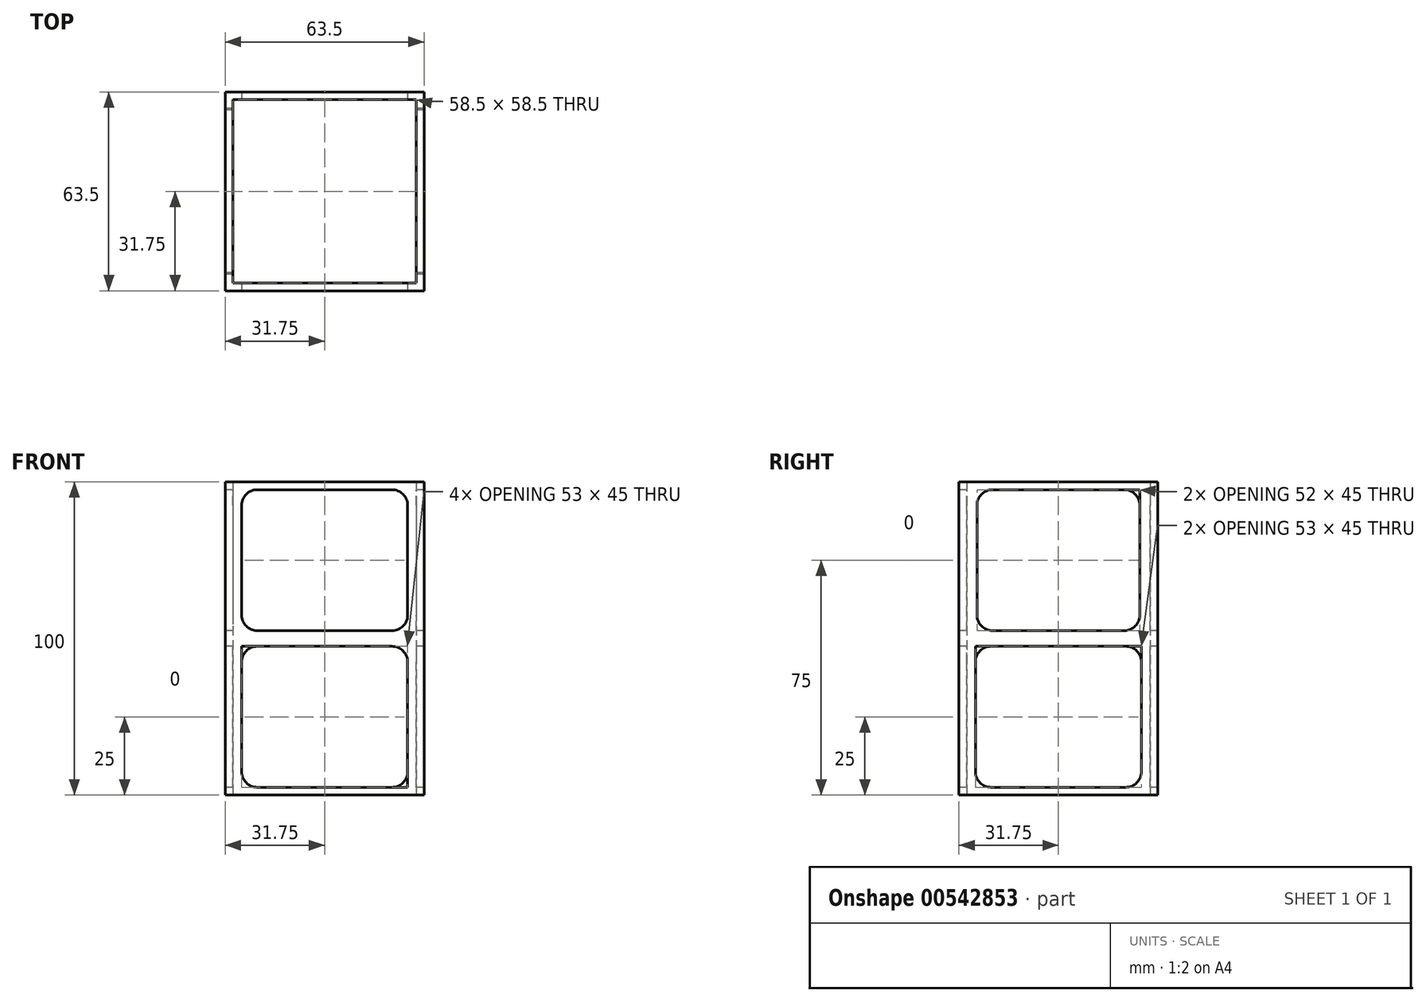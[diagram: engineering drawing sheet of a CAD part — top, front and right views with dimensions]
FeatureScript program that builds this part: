
annotation { "Feature Type Name" : "Feature", "Feature Type Description" : "" }
export const myFeature = defineFeature(function(context is Context, id is Id, definition is map)
    precondition{}
    {
        {
            var Q0;
            Q0=qCreatedBy(makeId("Top.planeOp"),FACE);
            var sketch = newSketch(context, id + "F0", { "sketchPlane" : qUnion([Q0])});
            skLineSegment(sketch, "E0.bottom", {"start": v(31.75, -31.75) * mm, "end": v(-31.75, -31.75) * mm});
            skLineSegment(sketch, "E0.top", {"start": v(31.75, 31.75) * mm, "end": v(-31.75, 31.75) * mm});
            skLineSegment(sketch, "E0.left", {"start": v(31.75, -31.75) * mm, "end": v(31.75, 31.75) * mm});
            skLineSegment(sketch, "E0.right", {"start": v(-31.75, -31.75) * mm, "end": v(-31.75, 31.75) * mm});
            skPoint(sketch, "E0.middle", {"position": v(0, 0) * mm});
            skLineSegment(sketch, "E1.bottom", {"start": v(29.25, -29.25) * mm, "end": v(-29.25, -29.25) * mm});
            skLineSegment(sketch, "E1.top", {"start": v(29.25, 29.25) * mm, "end": v(-29.25, 29.25) * mm});
            skLineSegment(sketch, "E1.left", {"start": v(29.25, -29.25) * mm, "end": v(29.25, 29.25) * mm});
            skLineSegment(sketch, "E1.right", {"start": v(-29.25, -29.25) * mm, "end": v(-29.25, 29.25) * mm});
            skSolve(sketch);
        }
        {
            var Q0;
            Q0=makeQuery(id+"F0.imprint","IMPRINT",FACE,{"disambiguationData":[TD([[makeQuery(id+"F0.imprint","IMPRINT",EDGE,{"derivedFrom":sQuery(id+"F0.wireOp",EDGE,"E0.bottom")}),-1.0]])]});
            extrude(context, id + "F1", {"entities" : qUnion([Q0]), "depth" : 100 * mm, "offsetDistance" : 25.4 * mm});
        }
        {
            var Q0;
            Q0=makeQuery(id+"F1.opExtrude","SWEPT_FACE",FACE,{"disambiguationData":[OSD([sQuery(id+"F0.wireOp",EDGE,"E0.bottom")])]});
            var sketch = newSketch(context, id + "F2", { "sketchPlane" : qUnion([Q0])});
            skLineSegment(sketch, "E2.bottom", {"start": v(26.5, 52.5) * mm, "end": v(-26.5, 52.5) * mm});
            skLineSegment(sketch, "E2.top", {"start": v(26.5, 97.5) * mm, "end": v(-26.5, 97.5) * mm});
            skLineSegment(sketch, "E2.left", {"start": v(26.5, 52.5) * mm, "end": v(26.5, 97.5) * mm});
            skLineSegment(sketch, "E2.right", {"start": v(-26.5, 52.5) * mm, "end": v(-26.5, 97.5) * mm});
            skPoint(sketch, "E2.middle", {"position": v(0, 75) * mm});
            skLineSegment(sketch, "E3.bottom", {"start": v(26.5, 2.5) * mm, "end": v(-26.5, 2.5) * mm});
            skLineSegment(sketch, "E3.top", {"start": v(26.5, 47.5) * mm, "end": v(-26.5, 47.5) * mm});
            skLineSegment(sketch, "E3.left", {"start": v(26.5, 2.5) * mm, "end": v(26.5, 47.5) * mm});
            skLineSegment(sketch, "E3.right", {"start": v(-26.5, 2.5) * mm, "end": v(-26.5, 47.5) * mm});
            skPoint(sketch, "E3.middle", {"position": v(0, 25) * mm});
            skSolve(sketch);
        }
        {
            var Q0;
            Q0=makeQuery(id+"F2.imprint","IMPRINT",FACE,{"disambiguationData":[TD([[makeQuery(id+"F2.imprint","IMPRINT",EDGE,{"derivedFrom":sQuery(id+"F2.wireOp",EDGE,"E2.bottom")}),-1.0]])]});
            var Q1;
            Q1=makeQuery(id+"F2.imprint","IMPRINT",FACE,{"disambiguationData":[TD([[makeQuery(id+"F2.imprint","IMPRINT",EDGE,{"derivedFrom":sQuery(id+"F2.wireOp",EDGE,"E3.bottom")}),-1.0]])]});
            extrude(context, id + "F3", {"entities" : qUnion([Q0, Q1]), "operationType" : NewBodyOperationType.REMOVE, "endBound" : BoundingType.THROUGH_ALL, "oppositeDirection" : true, "depth" : 25 * mm, "offsetDistance" : 25 * mm});
        }
        {
            var Q0;
            Q0=makeQuery(id+"F1.opExtrude","SWEPT_FACE",FACE,{"disambiguationData":[OSD([sQuery(id+"F0.wireOp",EDGE,"E0.right")])]});
            var sketch = newSketch(context, id + "F4", { "sketchPlane" : qUnion([Q0])});
            skLineSegment(sketch, "E4.bottom", {"start": v(26, 97.5) * mm, "end": v(-26, 97.5) * mm});
            skLineSegment(sketch, "E4.top", {"start": v(-26, 52.5) * mm, "end": v(26, 52.5) * mm});
            skLineSegment(sketch, "E4.left", {"start": v(26, 97.5) * mm, "end": v(26, 52.5) * mm});
            skLineSegment(sketch, "E4.right", {"start": v(-26, 97.5) * mm, "end": v(-26, 52.5) * mm});
            skPoint(sketch, "E4.middle", {"position": v(0, 75) * mm});
            skLineSegment(sketch, "E5.bottom", {"start": v(26.5, 2.5) * mm, "end": v(-26.5, 2.5) * mm});
            skLineSegment(sketch, "E5.top", {"start": v(26.5, 47.5) * mm, "end": v(-26.5, 47.5) * mm});
            skLineSegment(sketch, "E5.left", {"start": v(26.5, 2.5) * mm, "end": v(26.5, 47.5) * mm});
            skLineSegment(sketch, "E5.right", {"start": v(-26.5, 2.5) * mm, "end": v(-26.5, 47.5) * mm});
            skPoint(sketch, "E5.middle", {"position": v(0, 25) * mm});
            skSolve(sketch);
        }
        {
            var Q0;
            Q0=makeQuery(id+"F4.imprint","IMPRINT",FACE,{"disambiguationData":[TD([[makeQuery(id+"F4.imprint","IMPRINT",EDGE,{"derivedFrom":sQuery(id+"F4.wireOp",EDGE,"E5.bottom")}),-1.0]])]});
            var Q1;
            Q1=makeQuery(id+"F4.imprint","IMPRINT",FACE,{"disambiguationData":[TD([[makeQuery(id+"F4.imprint","IMPRINT",EDGE,{"derivedFrom":sQuery(id+"F4.wireOp",EDGE,"E4.bottom")}),1.0]])]});
            extrude(context, id + "F5", {"entities" : qUnion([Q0, Q1]), "operationType" : NewBodyOperationType.REMOVE, "endBound" : BoundingType.THROUGH_ALL, "oppositeDirection" : true, "depth" : 100 * mm, "offsetDistance" : 25 * mm});
        }
        {
            var Q0;
            {var subQ0=sQuery(id+"F4.wireOp",EDGE,"E5.bottom");var subQ1=sQuery(id+"F4.wireOp",EDGE,"E5.left");Q0=makeQuery(id+"F5.boolean.opBoolean","COPY",EDGE,{"disambiguationData":[TD([makeQuery(id+"F1.opExtrude","SWEPT_FACE",FACE,{"disambiguationData":[OSD([sQuery(id+"F0.wireOp",EDGE,"E0.left")])]})])],"derivedFrom":makeQuery(id+"F5.opExtrude","SWEPT_EDGE",EDGE,{"disambiguationData":[OSD([subQ0,subQ1])]})});}
            var Q1;
            {var subQ0=sQuery(id+"F4.wireOp",EDGE,"E4.top");var subQ1=sQuery(id+"F4.wireOp",EDGE,"E4.left");Q1=makeQuery(id+"F5.boolean.opBoolean","COPY",EDGE,{"disambiguationData":[TD([makeQuery(id+"F1.opExtrude","SWEPT_FACE",FACE,{"disambiguationData":[OSD([sQuery(id+"F0.wireOp",EDGE,"E0.left")])]})])],"derivedFrom":makeQuery(id+"F5.opExtrude","SWEPT_EDGE",EDGE,{"disambiguationData":[OSD([subQ0,subQ1])]})});}
            var Q2;
            {var subQ0=sQuery(id+"F2.wireOp",EDGE,"E3.bottom");var subQ1=sQuery(id+"F2.wireOp",EDGE,"E3.right");Q2=makeQuery(id+"F3.boolean.opBoolean","COPY",EDGE,{"disambiguationData":[TD([makeQuery(id+"F1.opExtrude","SWEPT_FACE",FACE,{"disambiguationData":[OSD([sQuery(id+"F0.wireOp",EDGE,"E0.top")])]})])],"derivedFrom":makeQuery(id+"F3.opExtrude","SWEPT_EDGE",EDGE,{"disambiguationData":[OSD([subQ0,subQ1])]})});}
            var Q3;
            {var subQ0=sQuery(id+"F4.wireOp",EDGE,"E5.bottom");var subQ1=sQuery(id+"F4.wireOp",EDGE,"E5.right");Q3=makeQuery(id+"F5.boolean.opBoolean","COPY",EDGE,{"disambiguationData":[TD([makeQuery(id+"F1.opExtrude","SWEPT_FACE",FACE,{"disambiguationData":[OSD([sQuery(id+"F0.wireOp",EDGE,"E0.right")])]})])],"derivedFrom":makeQuery(id+"F5.opExtrude","SWEPT_EDGE",EDGE,{"disambiguationData":[OSD([subQ0,subQ1])]})});}
            var Q4;
            {var subQ0=sQuery(id+"F2.wireOp",EDGE,"E3.bottom");var subQ1=sQuery(id+"F2.wireOp",EDGE,"E3.right");Q4=makeQuery(id+"F3.boolean.opBoolean","COPY",EDGE,{"disambiguationData":[TD([makeQuery(id+"F1.opExtrude","SWEPT_FACE",FACE,{"disambiguationData":[OSD([sQuery(id+"F0.wireOp",EDGE,"E0.bottom")])]})])],"derivedFrom":makeQuery(id+"F3.opExtrude","SWEPT_EDGE",EDGE,{"disambiguationData":[OSD([subQ0,subQ1])]})});}
            var Q5;
            {var subQ0=sQuery(id+"F2.wireOp",EDGE,"E2.bottom");var subQ1=sQuery(id+"F2.wireOp",EDGE,"E2.right");Q5=makeQuery(id+"F3.boolean.opBoolean","COPY",EDGE,{"disambiguationData":[TD([makeQuery(id+"F1.opExtrude","SWEPT_FACE",FACE,{"disambiguationData":[OSD([sQuery(id+"F0.wireOp",EDGE,"E0.bottom")])]})])],"derivedFrom":makeQuery(id+"F3.opExtrude","SWEPT_EDGE",EDGE,{"disambiguationData":[OSD([subQ0,subQ1])]})});}
            var Q6;
            {var subQ0=sQuery(id+"F2.wireOp",EDGE,"E2.bottom");var subQ1=sQuery(id+"F2.wireOp",EDGE,"E2.right");Q6=makeQuery(id+"F3.boolean.opBoolean","COPY",EDGE,{"disambiguationData":[TD([makeQuery(id+"F1.opExtrude","SWEPT_FACE",FACE,{"disambiguationData":[OSD([sQuery(id+"F0.wireOp",EDGE,"E0.top")])]})])],"derivedFrom":makeQuery(id+"F3.opExtrude","SWEPT_EDGE",EDGE,{"disambiguationData":[OSD([subQ0,subQ1])]})});}
            var Q7;
            {var subQ0=sQuery(id+"F4.wireOp",EDGE,"E4.top");var subQ1=sQuery(id+"F4.wireOp",EDGE,"E4.right");Q7=makeQuery(id+"F5.boolean.opBoolean","COPY",EDGE,{"disambiguationData":[TD([makeQuery(id+"F1.opExtrude","SWEPT_FACE",FACE,{"disambiguationData":[OSD([sQuery(id+"F0.wireOp",EDGE,"E0.right")])]})])],"derivedFrom":makeQuery(id+"F5.opExtrude","SWEPT_EDGE",EDGE,{"disambiguationData":[OSD([subQ0,subQ1])]})});}
            var Q8;
            {var subQ0=sQuery(id+"F4.wireOp",EDGE,"E4.top");var subQ1=sQuery(id+"F4.wireOp",EDGE,"E4.right");Q8=makeQuery(id+"F5.boolean.opBoolean","COPY",EDGE,{"disambiguationData":[TD([makeQuery(id+"F1.opExtrude","SWEPT_FACE",FACE,{"disambiguationData":[OSD([sQuery(id+"F0.wireOp",EDGE,"E0.left")])]})])],"derivedFrom":makeQuery(id+"F5.opExtrude","SWEPT_EDGE",EDGE,{"disambiguationData":[OSD([subQ0,subQ1])]})});}
            var Q9;
            {var subQ0=sQuery(id+"F2.wireOp",EDGE,"E3.bottom");var subQ1=sQuery(id+"F2.wireOp",EDGE,"E3.left");Q9=makeQuery(id+"F3.boolean.opBoolean","COPY",EDGE,{"disambiguationData":[TD([makeQuery(id+"F1.opExtrude","SWEPT_FACE",FACE,{"disambiguationData":[OSD([sQuery(id+"F0.wireOp",EDGE,"E0.bottom")])]})])],"derivedFrom":makeQuery(id+"F3.opExtrude","SWEPT_EDGE",EDGE,{"disambiguationData":[OSD([subQ0,subQ1])]})});}
            var Q10;
            {var subQ0=sQuery(id+"F2.wireOp",EDGE,"E2.bottom");var subQ1=sQuery(id+"F2.wireOp",EDGE,"E2.left");Q10=makeQuery(id+"F3.boolean.opBoolean","COPY",EDGE,{"disambiguationData":[TD([makeQuery(id+"F1.opExtrude","SWEPT_FACE",FACE,{"disambiguationData":[OSD([sQuery(id+"F0.wireOp",EDGE,"E0.bottom")])]})])],"derivedFrom":makeQuery(id+"F3.opExtrude","SWEPT_EDGE",EDGE,{"disambiguationData":[OSD([subQ0,subQ1])]})});}
            var Q11;
            {var subQ0=sQuery(id+"F2.wireOp",EDGE,"E2.bottom");var subQ1=sQuery(id+"F2.wireOp",EDGE,"E2.left");Q11=makeQuery(id+"F3.boolean.opBoolean","COPY",EDGE,{"disambiguationData":[TD([makeQuery(id+"F1.opExtrude","SWEPT_FACE",FACE,{"disambiguationData":[OSD([sQuery(id+"F0.wireOp",EDGE,"E0.top")])]})])],"derivedFrom":makeQuery(id+"F3.opExtrude","SWEPT_EDGE",EDGE,{"disambiguationData":[OSD([subQ0,subQ1])]})});}
            var Q12;
            {var subQ0=sQuery(id+"F4.wireOp",EDGE,"E5.bottom");var subQ1=sQuery(id+"F4.wireOp",EDGE,"E5.left");Q12=makeQuery(id+"F5.boolean.opBoolean","COPY",EDGE,{"disambiguationData":[TD([makeQuery(id+"F1.opExtrude","SWEPT_FACE",FACE,{"disambiguationData":[OSD([sQuery(id+"F0.wireOp",EDGE,"E0.right")])]})])],"derivedFrom":makeQuery(id+"F5.opExtrude","SWEPT_EDGE",EDGE,{"disambiguationData":[OSD([subQ0,subQ1])]})});}
            var Q13;
            {var subQ0=sQuery(id+"F4.wireOp",EDGE,"E4.top");var subQ1=sQuery(id+"F4.wireOp",EDGE,"E4.left");Q13=makeQuery(id+"F5.boolean.opBoolean","COPY",EDGE,{"disambiguationData":[TD([makeQuery(id+"F1.opExtrude","SWEPT_FACE",FACE,{"disambiguationData":[OSD([sQuery(id+"F0.wireOp",EDGE,"E0.right")])]})])],"derivedFrom":makeQuery(id+"F5.opExtrude","SWEPT_EDGE",EDGE,{"disambiguationData":[OSD([subQ0,subQ1])]})});}
            fillet(context, id + "F6", {"entities" : qUnion([Q0, Q1, Q2, Q3, Q4, Q5, Q6, Q7, Q8, Q9, Q10, Q11, Q12, Q13]), "radius" : 5 * mm, "tangentPropagation" : true, "allowEdgeOverflow" : false});
        }
        {
            var Q0;
            {var subQ0=sQuery(id+"F4.wireOp",EDGE,"E4.bottom");var subQ1=sQuery(id+"F4.wireOp",EDGE,"E4.right");Q0=makeQuery(id+"F5.boolean.opBoolean","COPY",EDGE,{"disambiguationData":[TD([makeQuery(id+"F1.opExtrude","SWEPT_FACE",FACE,{"disambiguationData":[OSD([sQuery(id+"F0.wireOp",EDGE,"E0.left")])]})])],"derivedFrom":makeQuery(id+"F5.opExtrude","SWEPT_EDGE",EDGE,{"disambiguationData":[OSD([subQ0,subQ1])]})});}
            var Q1;
            {var subQ0=sQuery(id+"F4.wireOp",EDGE,"E5.right");var subQ1=sQuery(id+"F4.wireOp",EDGE,"E5.top");Q1=makeQuery(id+"F5.boolean.opBoolean","COPY",EDGE,{"disambiguationData":[TD([makeQuery(id+"F1.opExtrude","SWEPT_FACE",FACE,{"disambiguationData":[OSD([sQuery(id+"F0.wireOp",EDGE,"E0.left")])]})])],"derivedFrom":makeQuery(id+"F5.opExtrude","SWEPT_EDGE",EDGE,{"disambiguationData":[OSD([subQ1,subQ0])]})});}
            var Q2;
            {var subQ0=sQuery(id+"F2.wireOp",EDGE,"E3.top");var subQ1=sQuery(id+"F2.wireOp",EDGE,"E3.right");Q2=makeQuery(id+"F3.boolean.opBoolean","COPY",EDGE,{"disambiguationData":[TD([makeQuery(id+"F1.opExtrude","SWEPT_FACE",FACE,{"disambiguationData":[OSD([sQuery(id+"F0.wireOp",EDGE,"E0.bottom")])]})])],"derivedFrom":makeQuery(id+"F3.opExtrude","SWEPT_EDGE",EDGE,{"disambiguationData":[OSD([subQ0,subQ1])]})});}
            var Q3;
            {var subQ0=sQuery(id+"F2.wireOp",EDGE,"E2.top");var subQ1=sQuery(id+"F2.wireOp",EDGE,"E2.right");Q3=makeQuery(id+"F3.boolean.opBoolean","COPY",EDGE,{"disambiguationData":[TD([makeQuery(id+"F1.opExtrude","SWEPT_FACE",FACE,{"disambiguationData":[OSD([sQuery(id+"F0.wireOp",EDGE,"E0.bottom")])]})])],"derivedFrom":makeQuery(id+"F3.opExtrude","SWEPT_EDGE",EDGE,{"disambiguationData":[OSD([subQ0,subQ1])]})});}
            var Q4;
            {var subQ0=sQuery(id+"F4.wireOp",EDGE,"E5.bottom");var subQ1=sQuery(id+"F4.wireOp",EDGE,"E5.right");Q4=makeQuery(id+"F5.boolean.opBoolean","COPY",EDGE,{"disambiguationData":[TD([makeQuery(id+"F1.opExtrude","SWEPT_FACE",FACE,{"disambiguationData":[OSD([sQuery(id+"F0.wireOp",EDGE,"E0.left")])]})])],"derivedFrom":makeQuery(id+"F5.opExtrude","SWEPT_EDGE",EDGE,{"disambiguationData":[OSD([subQ0,subQ1])]})});}
            var Q5;
            {var subQ0=sQuery(id+"F2.wireOp",EDGE,"E2.right");var subQ1=sQuery(id+"F2.wireOp",EDGE,"E2.top");Q5=makeQuery(id+"F3.boolean.opBoolean","COPY",EDGE,{"disambiguationData":[TD([makeQuery(id+"F1.opExtrude","SWEPT_FACE",FACE,{"disambiguationData":[OSD([sQuery(id+"F0.wireOp",EDGE,"E0.top")])]})])],"derivedFrom":makeQuery(id+"F3.opExtrude","SWEPT_EDGE",EDGE,{"disambiguationData":[OSD([subQ1,subQ0])]})});}
            var Q6;
            {var subQ0=sQuery(id+"F2.wireOp",EDGE,"E2.left");var subQ1=sQuery(id+"F2.wireOp",EDGE,"E2.top");Q6=makeQuery(id+"F3.boolean.opBoolean","COPY",EDGE,{"disambiguationData":[TD([makeQuery(id+"F1.opExtrude","SWEPT_FACE",FACE,{"disambiguationData":[OSD([sQuery(id+"F0.wireOp",EDGE,"E0.top")])]})])],"derivedFrom":makeQuery(id+"F3.opExtrude","SWEPT_EDGE",EDGE,{"disambiguationData":[OSD([subQ1,subQ0])]})});}
            var Q7;
            {var subQ0=sQuery(id+"F4.wireOp",EDGE,"E4.bottom");var subQ1=sQuery(id+"F4.wireOp",EDGE,"E4.left");Q7=makeQuery(id+"F5.boolean.opBoolean","COPY",EDGE,{"disambiguationData":[TD([makeQuery(id+"F1.opExtrude","SWEPT_FACE",FACE,{"disambiguationData":[OSD([sQuery(id+"F0.wireOp",EDGE,"E0.left")])]})])],"derivedFrom":makeQuery(id+"F5.opExtrude","SWEPT_EDGE",EDGE,{"disambiguationData":[OSD([subQ0,subQ1])]})});}
            var Q8;
            {var subQ0=sQuery(id+"F2.wireOp",EDGE,"E2.top");var subQ1=sQuery(id+"F2.wireOp",EDGE,"E2.left");Q8=makeQuery(id+"F3.boolean.opBoolean","COPY",EDGE,{"disambiguationData":[TD([makeQuery(id+"F1.opExtrude","SWEPT_FACE",FACE,{"disambiguationData":[OSD([sQuery(id+"F0.wireOp",EDGE,"E0.bottom")])]})])],"derivedFrom":makeQuery(id+"F3.opExtrude","SWEPT_EDGE",EDGE,{"disambiguationData":[OSD([subQ0,subQ1])]})});}
            var Q9;
            {var subQ0=sQuery(id+"F4.wireOp",EDGE,"E5.top");var subQ1=sQuery(id+"F4.wireOp",EDGE,"E5.left");Q9=makeQuery(id+"F5.boolean.opBoolean","COPY",EDGE,{"disambiguationData":[TD([makeQuery(id+"F1.opExtrude","SWEPT_FACE",FACE,{"disambiguationData":[OSD([sQuery(id+"F0.wireOp",EDGE,"E0.left")])]})])],"derivedFrom":makeQuery(id+"F5.opExtrude","SWEPT_EDGE",EDGE,{"disambiguationData":[OSD([subQ0,subQ1])]})});}
            var Q10;
            {var subQ0=sQuery(id+"F2.wireOp",EDGE,"E3.top");var subQ1=sQuery(id+"F2.wireOp",EDGE,"E3.left");Q10=makeQuery(id+"F3.boolean.opBoolean","COPY",EDGE,{"disambiguationData":[TD([makeQuery(id+"F1.opExtrude","SWEPT_FACE",FACE,{"disambiguationData":[OSD([sQuery(id+"F0.wireOp",EDGE,"E0.bottom")])]})])],"derivedFrom":makeQuery(id+"F3.opExtrude","SWEPT_EDGE",EDGE,{"disambiguationData":[OSD([subQ0,subQ1])]})});}
            var Q11;
            {var subQ0=sQuery(id+"F2.wireOp",EDGE,"E3.left");var subQ1=sQuery(id+"F2.wireOp",EDGE,"E3.top");Q11=makeQuery(id+"F3.boolean.opBoolean","COPY",EDGE,{"disambiguationData":[TD([makeQuery(id+"F1.opExtrude","SWEPT_FACE",FACE,{"disambiguationData":[OSD([sQuery(id+"F0.wireOp",EDGE,"E0.top")])]})])],"derivedFrom":makeQuery(id+"F3.opExtrude","SWEPT_EDGE",EDGE,{"disambiguationData":[OSD([subQ1,subQ0])]})});}
            var Q12;
            {var subQ0=sQuery(id+"F4.wireOp",EDGE,"E4.bottom");var subQ1=sQuery(id+"F4.wireOp",EDGE,"E4.left");Q12=makeQuery(id+"F5.boolean.opBoolean","COPY",EDGE,{"disambiguationData":[TD([makeQuery(id+"F1.opExtrude","SWEPT_FACE",FACE,{"disambiguationData":[OSD([sQuery(id+"F0.wireOp",EDGE,"E0.right")])]})])],"derivedFrom":makeQuery(id+"F5.opExtrude","SWEPT_EDGE",EDGE,{"disambiguationData":[OSD([subQ0,subQ1])]})});}
            fillet(context, id + "F7", {"entities" : qUnion([Q0, Q1, Q2, Q3, Q4, Q5, Q6, Q7, Q8, Q9, Q10, Q11, Q12]), "radius" : 5 * mm, "tangentPropagation" : true, "allowEdgeOverflow" : false});
        }
    });
